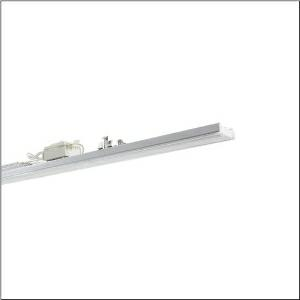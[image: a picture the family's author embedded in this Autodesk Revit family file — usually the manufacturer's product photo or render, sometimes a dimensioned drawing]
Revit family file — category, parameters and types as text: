
# Revit family: licross_r__21_recessed_ho_52tl12dn4fxmd_dc4c
name_source: partatom
category: Lighting Fixtures
units: mm (PartAtom-declared; Revit-internal decimal feet)

## family parameters
Cut with Voids When Loaded = No
Host = Face
Light Source = No
Part Type = Normal
Room Calculation Point = No
Round Connector Dimension = Use Diameter
Shared = No

## types (1)
- --- (1 x LED, 2250 lm, 14 W, 4000K)
    Apparent Load = 14 VA
    CIE Flux Codes = 69 91 98 100 100
    Color Rendering = 80
    Color Temperature = 4000K
    Default Elevation = 1800 mm
    Description = Licross® 21 Recessed HO, luminaire insert, of sheet steel, galvanised, coil coated, white, length: 1.500mm, width: 66mm, height: 67mm, LED rated luminous flux: 15.000lm, light colour: 840, control gear: DALI 2 (for two DALI lines), with plug, 6-pole, with phase selection, mains connection: 220..240V, AC/DC, 0/50..60Hz, rated input power: 85W, without changeover relay, for emergency light function, for central battery installations according to DIN EN 60598-2-22, halogen-free wiring, primary optical cover: cover, of PMMA, light emission: direct distribution, primary light characteristic: symmetric, protection rating (complete): IP40, insulation class (complete): insulation class I (protective earthing), certification: CE, ENEC, VDE, UKCA, protection symbol: D if used in an environment without relevant dust loads with corresponding accessories, impact resistance: IK06, permissible ambient temperature for indoor applications: -25..+30°C, standard: EN 60598-2-22, corresponds to IFS (International Featured Standards) requirements for safety and quality in the food industry, reducing of maximum allowable ambient temperature of 5°C with ceiling mounting, LABS conformity tested according to VDMA 24364:2018-05, packaging unit: 1 piece
    Height = 58 mm
    Lamp = 1 x LED
    Lamp Light Flux = 2250 lm
    Lamp Power = 14 W
    Lamp count = 1
    Length = 1500 mm
    Luminous efficacy = 161 lm/W
    Manufacturer = Siteco
    ModVariant = No
    Model = 52TL12DN4FXMD
    Mounting Place = Ceiling
    Mounting Type = Pendant
    Number of Poles = 1
    OnlyDefault = Yes
    Power Factor = 1
    Product Name = Licross® 21 Recessed HO
    Product group = luminaire insert
    ProductGroupID = 902
    Protection Class = Protection class I
    Protection Degree = IP 40
    RLX_Detail_Level = 1
    RLX_Emergency_Light_Flux = 0 lm
    RLX_Emergency_Type = 0
    RLX_Emergency_Type_DB = No
    RlxData = <blob elided: 25145 chars, md5=065f34db>
    Socket = socket
    Standby Power = 0 W
    System Light Flux = 2250 lm
    System Power = 14 W
    Type Comments = : DC mode (central or group accumulator) initial emergency light level
    Type Image = l_1296930.jpg
    URL = http://relux.com
    VarID = @adj_111770
    Voltage = 0 V
    Weight = 0.00 kg
    Width = 66 mm

## geometry (parser evidence)
native form markers: Blend x4, Sweep x12
no freeform markers — native parametric forms only
